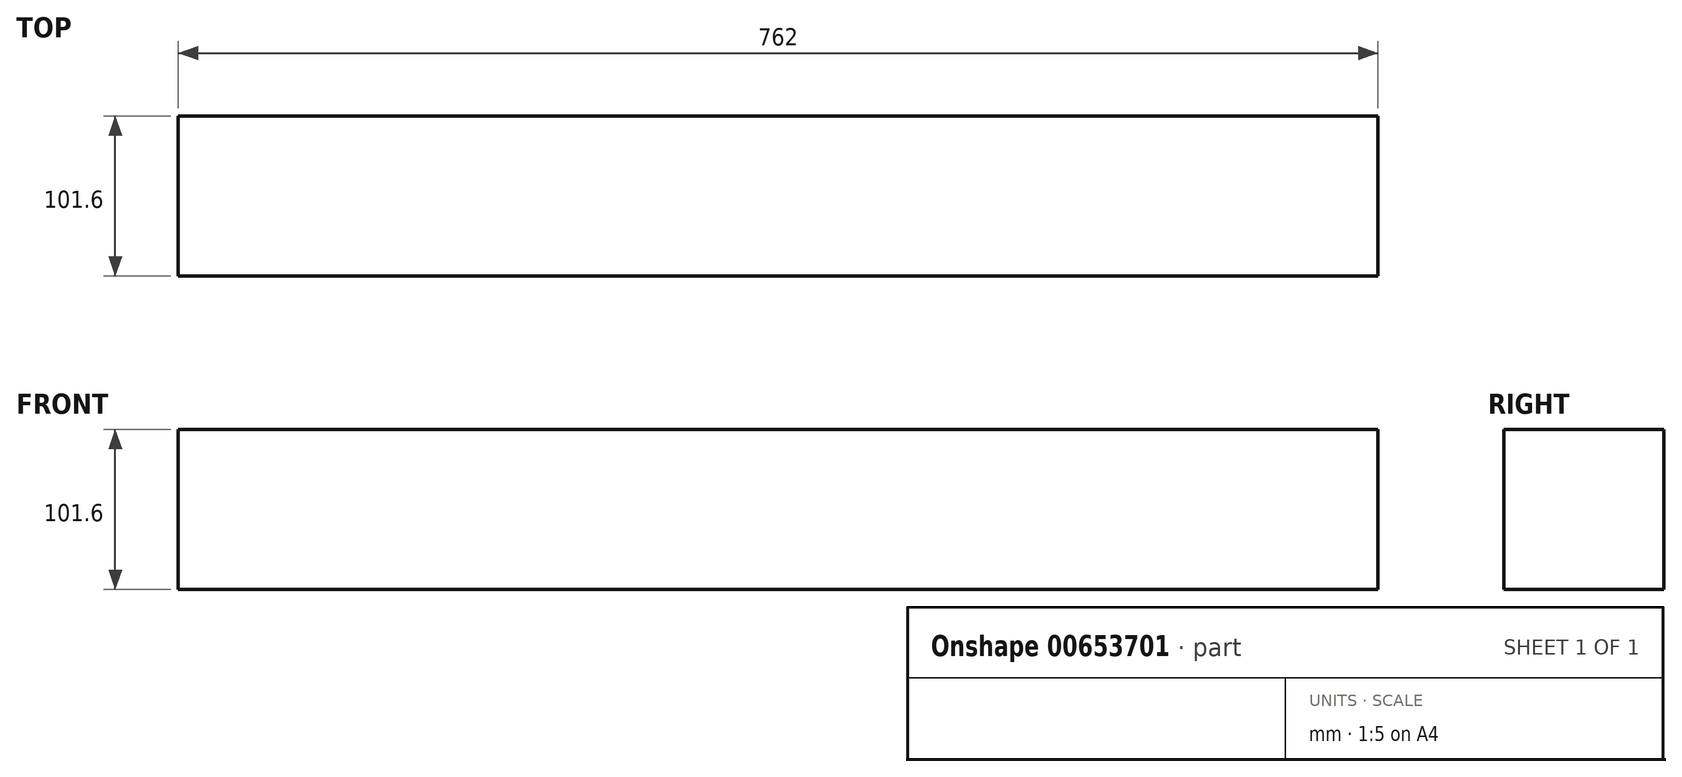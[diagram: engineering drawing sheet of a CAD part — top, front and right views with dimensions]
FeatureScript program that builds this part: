
annotation { "Feature Type Name" : "Feature", "Feature Type Description" : "" }
export const myFeature = defineFeature(function(context is Context, id is Id, definition is map)
    precondition{}
    {
        {
            var Q0;
            Q0=qCreatedBy(makeId("Right.planeOp"),FACE);
            var sketch = newSketch(context, id + "F0", { "sketchPlane" : qUnion([Q0])});
            skLineSegment(sketch, "E0.bottom", {"start": v(-78.8, 79.03) * mm, "end": v(22.8, 79.03) * mm});
            skLineSegment(sketch, "E0.top", {"start": v(-78.8, -22.57) * mm, "end": v(22.8, -22.57) * mm});
            skLineSegment(sketch, "E0.left", {"start": v(-78.8, 79.03) * mm, "end": v(-78.8, -22.57) * mm});
            skLineSegment(sketch, "E0.right", {"start": v(22.8, 79.03) * mm, "end": v(22.8, -22.57) * mm});
            skSolve(sketch);
        }
        {
            var Q0;
            Q0=makeQuery(id+"F0.imprint","IMPRINT",FACE,{"disambiguationData":[TD([[makeQuery(id+"F0.imprint","IMPRINT",EDGE,{"derivedFrom":sQuery(id+"F0.wireOp",EDGE,"E0.bottom")}),-1.0]])]});
            extrude(context, id + "F1", {"entities" : qUnion([Q0]), "depth" : 762 * mm, "offsetDistance" : 25.4 * mm});
        }
    });
